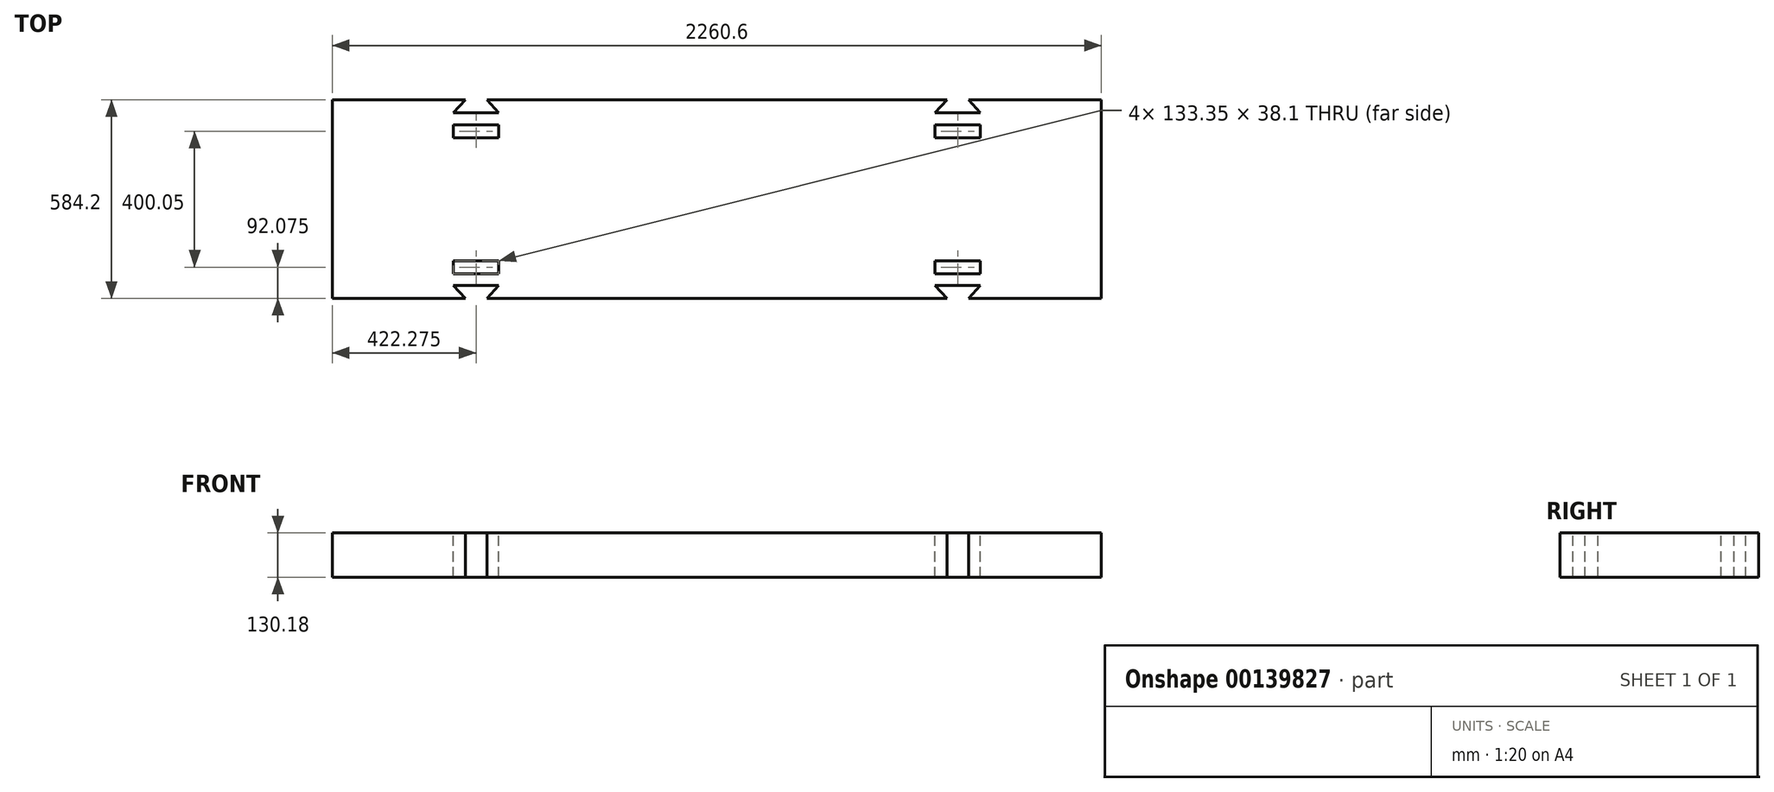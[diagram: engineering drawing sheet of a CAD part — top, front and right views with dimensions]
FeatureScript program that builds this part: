
annotation { "Feature Type Name" : "Feature", "Feature Type Description" : "" }
export const myFeature = defineFeature(function(context is Context, id is Id, definition is map)
    precondition{}
    {
        {
            var Q0;
            Q0=qCreatedBy(makeId("Top.planeOp"),FACE);
            var sketch = newSketch(context, id + "F0", { "sketchPlane" : qUnion([Q0])});
            skLineSegment(sketch, "E0.bottom", {"start": v(-1130.3, 292.1) * mm, "end": v(1130.3, 292.1) * mm});
            skLineSegment(sketch, "E0.top", {"start": v(-1130.3, -292.1) * mm, "end": v(1130.3, -292.1) * mm});
            skLineSegment(sketch, "E0.left", {"start": v(-1130.3, 292.1) * mm, "end": v(-1130.3, -292.1) * mm});
            skLineSegment(sketch, "E0.right", {"start": v(1130.3, 292.1) * mm, "end": v(1130.3, -292.1) * mm});
            skSolve(sketch);
        }
        {
            var Q0;
            Q0 = qSketchRegion(id + "F0", true);
            extrude(context, id + "F1", {"entities" : qUnion([Q0]), "depth" : 130.17 * mm});
        }
        {
            var Q0;
            Q0=makeQuery(id+"F1.opExtrude","CAP_FACE",FACE,{"disambiguationData":[OSD([sQuery(id+"F0.wireOp",EDGE,"E0.bottom"),sQuery(id+"F0.wireOp",EDGE,"E0.top"),sQuery(id+"F0.wireOp",EDGE,"E0.left"),sQuery(id+"F0.wireOp",EDGE,"E0.right")])],"isStart":false});
            var sketch = newSketch(context, id + "F2", { "sketchPlane" : qUnion([Q0])});
            skLineSegment(sketch, "E1.bottom", {"start": v(-774.7, -180.98) * mm, "end": v(-641.35, -180.98) * mm});
            skLineSegment(sketch, "E1.top", {"start": v(-774.7, -219.08) * mm, "end": v(-641.35, -219.08) * mm});
            skLineSegment(sketch, "E1.left", {"start": v(-774.7, -180.98) * mm, "end": v(-774.7, -219.08) * mm});
            skLineSegment(sketch, "E1.right", {"start": v(-641.35, -180.98) * mm, "end": v(-641.35, -219.08) * mm});
            skLineSegment(sketch, "E2", {"start": v(-641.35, -254) * mm, "end": v(-774.7, -254) * mm});
            skLineSegment(sketch, "E3", {"start": v(-774.7, -254) * mm, "end": v(-739.78, -292.1) * mm});
            skLineSegment(sketch, "E4", {"start": v(-739.78, -292.1) * mm, "end": v(-676.27, -292.1) * mm});
            skLineSegment(sketch, "E5", {"start": v(-676.28, -292.1) * mm, "end": v(-641.35, -254) * mm});
            skLineSegment(sketch, "E6.bottom", {"start": v(641.35, -180.98) * mm, "end": v(774.7, -180.98) * mm});
            skLineSegment(sketch, "E6.top", {"start": v(641.35, -219.08) * mm, "end": v(774.7, -219.08) * mm});
            skLineSegment(sketch, "E6.left", {"start": v(641.35, -180.98) * mm, "end": v(641.35, -219.08) * mm});
            skLineSegment(sketch, "E6.right", {"start": v(774.7, -180.98) * mm, "end": v(774.7, -219.08) * mm});
            skLineSegment(sketch, "E7", {"start": v(774.7, -254) * mm, "end": v(641.35, -254) * mm});
            skLineSegment(sketch, "E8", {"start": v(641.35, -254) * mm, "end": v(676.27, -292.1) * mm});
            skLineSegment(sketch, "E9", {"start": v(676.27, -292.1) * mm, "end": v(739.78, -292.1) * mm});
            skLineSegment(sketch, "E10", {"start": v(739.78, -292.1) * mm, "end": v(774.7, -254) * mm});
            skLineSegment(sketch, "E11.bottom", {"start": v(-641.35, 180.97) * mm, "end": v(-774.7, 180.97) * mm});
            skLineSegment(sketch, "E11.top", {"start": v(-641.35, 219.08) * mm, "end": v(-774.7, 219.08) * mm});
            skLineSegment(sketch, "E11.left", {"start": v(-641.35, 180.97) * mm, "end": v(-641.35, 219.07) * mm});
            skLineSegment(sketch, "E11.right", {"start": v(-774.7, 180.97) * mm, "end": v(-774.7, 219.07) * mm});
            skLineSegment(sketch, "E12", {"start": v(-774.7, 254) * mm, "end": v(-641.35, 254) * mm});
            skLineSegment(sketch, "E13", {"start": v(-641.35, 254) * mm, "end": v(-676.27, 292.1) * mm});
            skLineSegment(sketch, "E14", {"start": v(-676.27, 292.1) * mm, "end": v(-739.78, 292.1) * mm});
            skLineSegment(sketch, "E15", {"start": v(-739.78, 292.1) * mm, "end": v(-774.7, 254) * mm});
            skLineSegment(sketch, "E16.bottom", {"start": v(774.7, 180.98) * mm, "end": v(641.35, 180.98) * mm});
            skLineSegment(sketch, "E16.top", {"start": v(774.7, 219.08) * mm, "end": v(641.35, 219.08) * mm});
            skLineSegment(sketch, "E16.left", {"start": v(774.7, 180.98) * mm, "end": v(774.7, 219.08) * mm});
            skLineSegment(sketch, "E16.right", {"start": v(641.35, 180.98) * mm, "end": v(641.35, 219.08) * mm});
            skLineSegment(sketch, "E17", {"start": v(641.35, 254) * mm, "end": v(774.7, 254) * mm});
            skLineSegment(sketch, "E18", {"start": v(774.7, 254) * mm, "end": v(739.78, 292.1) * mm});
            skLineSegment(sketch, "E19", {"start": v(739.78, 292.1) * mm, "end": v(676.28, 292.1) * mm});
            skLineSegment(sketch, "E20", {"start": v(676.28, 292.1) * mm, "end": v(641.35, 254) * mm});
            skSolve(sketch);
        }
        {
            var Q0;
            Q0 = qSketchRegion(id + "F2", true);
            extrude(context, id + "F3", {"entities" : qUnion([Q0]), "operationType" : NewBodyOperationType.REMOVE, "oppositeDirection" : true, "depth" : 130.17 * mm});
        }
    });
